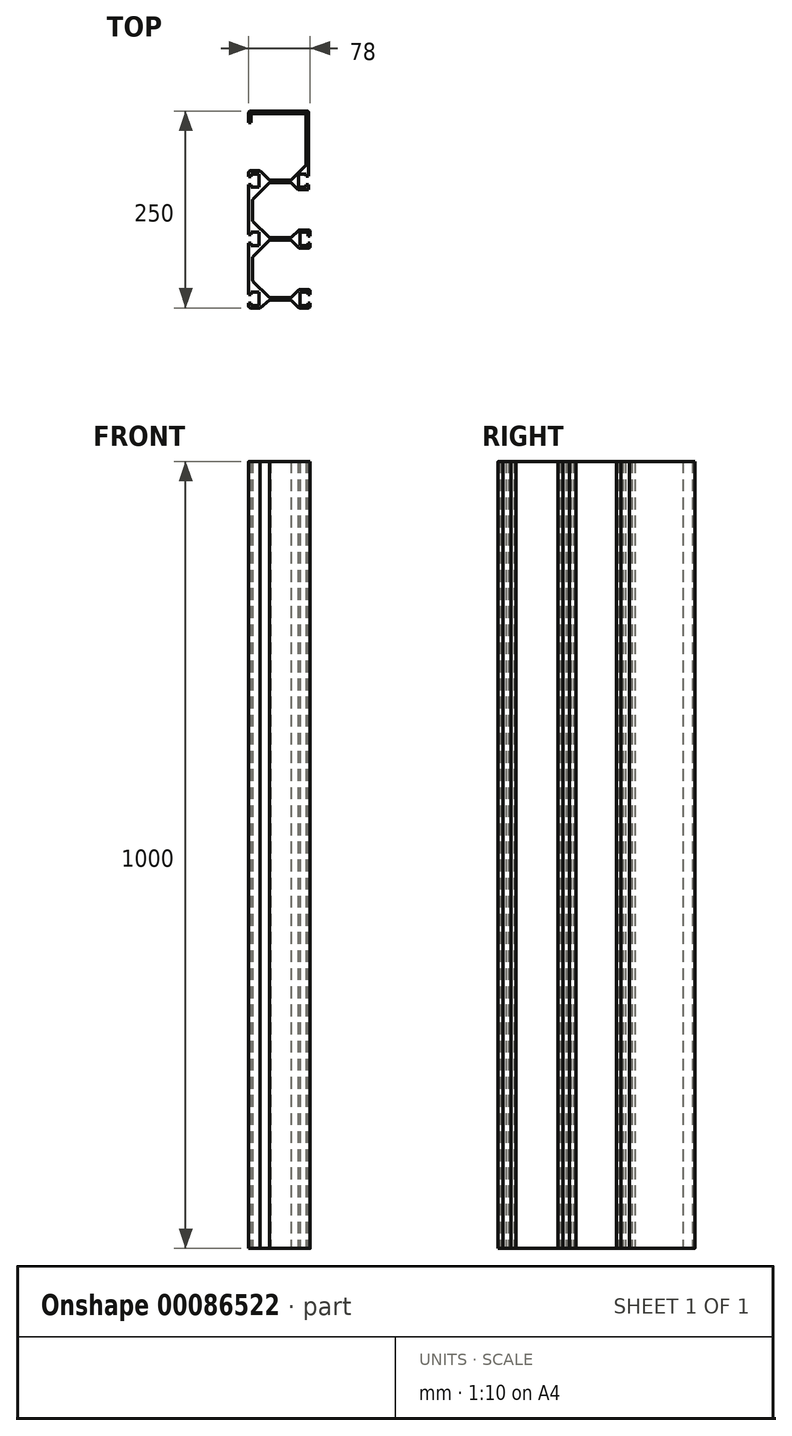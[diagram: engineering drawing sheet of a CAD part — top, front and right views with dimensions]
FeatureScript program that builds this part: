
annotation { "Feature Type Name" : "Feature", "Feature Type Description" : "" }
export const myFeature = defineFeature(function(context is Context, id is Id, definition is map)
    precondition{}
    {
        {
            var Q0;
            Q0=qCreatedBy(makeId("Top.planeOp"),FACE);
            var sketch = newSketch(context, id + "F0", { "sketchPlane" : qUnion([Q0])});
            skLineSegment(sketch, "E0", {"start": v(0, 3.75) * mm, "end": v(3, 3.75) * mm});
            skLineSegment(sketch, "E1", {"start": v(3, 3.75) * mm, "end": v(3, 7) * mm});
            skLineSegment(sketch, "E2", {"start": v(3, 7) * mm, "end": v(13, 7) * mm});
            skPoint(sketch, "E3.visualSharp", {"position": v(16, 0) * mm});
            skLineSegment(sketch, "E4", {"start": v(13, 7) * mm, "end": v(13, -10) * mm});
            skLineSegment(sketch, "E5", {"start": v(13, -10) * mm, "end": v(3, -10) * mm});
            skLineSegment(sketch, "E6", {"start": v(3, -10) * mm, "end": v(3, -6.75) * mm});
            skLineSegment(sketch, "E7", {"start": v(3, -6.75) * mm, "end": v(0, -6.75) * mm});
            skLineSegment(sketch, "E8", {"start": v(13, -67.17) * mm, "end": v(13, -84.17) * mm});
            skLineSegment(sketch, "E9", {"start": v(0, -6.75) * mm, "end": v(0, -70.42) * mm});
            skLineSegment(sketch, "E10", {"start": v(0, -70.42) * mm, "end": v(3, -70.42) * mm});
            skLineSegment(sketch, "E11", {"start": v(3, -70.42) * mm, "end": v(3, -67.17) * mm});
            skLineSegment(sketch, "E12", {"start": v(3, -67.17) * mm, "end": v(13, -67.17) * mm});
            skLineSegment(sketch, "E13", {"start": v(13, -84.17) * mm, "end": v(3, -84.17) * mm});
            skLineSegment(sketch, "E14", {"start": v(3, -84.17) * mm, "end": v(3, -80.92) * mm});
            skLineSegment(sketch, "E15", {"start": v(3, -80.92) * mm, "end": v(0, -80.92) * mm});
            skLineSegment(sketch, "E16", {"start": v(0, -80.92) * mm, "end": v(0, -146.42) * mm});
            skLineSegment(sketch, "E17", {"start": v(0, -146.42) * mm, "end": v(3, -146.42) * mm});
            skLineSegment(sketch, "E18", {"start": v(3, -146.42) * mm, "end": v(3, -143.17) * mm});
            skLineSegment(sketch, "E19", {"start": v(3, -143.17) * mm, "end": v(13, -143.17) * mm});
            skLineSegment(sketch, "E20", {"start": v(13, -143.17) * mm, "end": v(13, -160.17) * mm});
            skLineSegment(sketch, "E21", {"start": v(13, -160.17) * mm, "end": v(3, -160.17) * mm});
            skLineSegment(sketch, "E22", {"start": v(3, -160.17) * mm, "end": v(3, -156.92) * mm});
            skLineSegment(sketch, "E23", {"start": v(3, -156.92) * mm, "end": v(0, -156.92) * mm});
            skLineSegment(sketch, "E24", {"start": v(0, -156.92) * mm, "end": v(0, -161.17) * mm});
            skLineSegment(sketch, "E25", {"start": v(5.59, -129.54) * mm, "end": v(25.63, -149.59) * mm});
            skLineSegment(sketch, "E26", {"start": v(26.2, -77.18) * mm, "end": v(5.59, -97.8) * mm});
            skLineSegment(sketch, "E27", {"start": v(5, -128.13) * mm, "end": v(5, -99.21) * mm});
            skLineSegment(sketch, "E28", {"start": v(25.65, -73.63) * mm, "end": v(5.59, -53.54) * mm});
            skLineSegment(sketch, "E29", {"start": v(5, -26.21) * mm, "end": v(5, -52.13) * mm});
            skLineSegment(sketch, "E30", {"start": v(2, -163.17) * mm, "end": v(14.21, -163.17) * mm});
            skLineSegment(sketch, "E31", {"start": v(14.21, -163.17) * mm, "end": v(26.21, -153.17) * mm});
            skPoint(sketch, "E32.visualSharp", {"position": v(26.21, -150.17) * mm});
            skArc(sketch, "E32.filletArc", {"start": v(25.63, -149.59) * mm, "mid": v(26.28, -150.02) * mm, "end": v(27.04, -150.17) * mm});
            skPoint(sketch, "E33.visualSharp", {"position": v(5, -128.96) * mm});
            skArc(sketch, "E33.filletArc", {"start": v(5, -128.13) * mm, "mid": v(5.15, -128.9) * mm, "end": v(5.59, -129.54) * mm});
            skPoint(sketch, "E34.visualSharp", {"position": v(5, -98.39) * mm});
            skArc(sketch, "E34.filletArc", {"start": v(5.59, -97.8) * mm, "mid": v(5.15, -98.45) * mm, "end": v(5, -99.21) * mm});
            skPoint(sketch, "E35.visualSharp", {"position": v(26.21, -77.17) * mm});
            skArc(sketch, "E35.filletArc", {"start": v(26.21, -77.17) * mm, "mid": v(26.2, -77.18) * mm, "end": v(26.2, -77.18) * mm});
            skPoint(sketch, "E36.visualSharp", {"position": v(26.21, -74.2) * mm});
            skArc(sketch, "E36.filletArc", {"start": v(25.65, -73.63) * mm, "mid": v(26.49, -74.13) * mm, "end": v(27.46, -74.17) * mm});
            skPoint(sketch, "E37.visualSharp", {"position": v(5, -25.38) * mm});
            skArc(sketch, "E37.filletArc", {"start": v(5.59, -24.8) * mm, "mid": v(5.15, -25.45) * mm, "end": v(5, -26.21) * mm});
            skArc(sketch, "E38.filletArc", {"start": v(26.21, -4.17) * mm, "mid": v(26.2, -4.18) * mm, "end": v(26.2, -4.19) * mm});
            skPoint(sketch, "E39.visualSharp", {"position": v(5, -52.96) * mm});
            skArc(sketch, "E39.filletArc", {"start": v(5, -52.13) * mm, "mid": v(5.15, -52.9) * mm, "end": v(5.59, -53.54) * mm});
            skLineSegment(sketch, "E40", {"start": v(76, -163.17) * mm, "end": v(64.62, -163.17) * mm});
            skLineSegment(sketch, "E41", {"start": v(63.2, -162.59) * mm, "end": v(54.37, -153.76) * mm});
            skLineSegment(sketch, "E42", {"start": v(52.96, -153.17) * mm, "end": v(26.21, -153.17) * mm});
            skLineSegment(sketch, "E43", {"start": v(78, -161.17) * mm, "end": v(78, -156.92) * mm});
            skLineSegment(sketch, "E44", {"start": v(78, -156.92) * mm, "end": v(75, -156.92) * mm});
            skLineSegment(sketch, "E45", {"start": v(75, -156.92) * mm, "end": v(75, -160.17) * mm});
            skLineSegment(sketch, "E46", {"start": v(75, -160.17) * mm, "end": v(65, -160.17) * mm});
            skLineSegment(sketch, "E47", {"start": v(65, -160.17) * mm, "end": v(65, -143.17) * mm});
            skLineSegment(sketch, "E48", {"start": v(65, -143.17) * mm, "end": v(75, -143.17) * mm});
            skLineSegment(sketch, "E49", {"start": v(75, -143.17) * mm, "end": v(75, -146.42) * mm});
            skLineSegment(sketch, "E50", {"start": v(75, -146.42) * mm, "end": v(78, -146.42) * mm});
            skLineSegment(sketch, "E51", {"start": v(78, -146.42) * mm, "end": v(78, -142.17) * mm});
            skLineSegment(sketch, "E52", {"start": v(76, -140.17) * mm, "end": v(64.62, -140.17) * mm});
            skLineSegment(sketch, "E53", {"start": v(63.2, -140.76) * mm, "end": v(54.37, -149.59) * mm});
            skLineSegment(sketch, "E54", {"start": v(52.96, -150.17) * mm, "end": v(27.04, -150.17) * mm});
            skPoint(sketch, "E55.visualSharp", {"position": v(53.79, -150.17) * mm});
            skArc(sketch, "E55.filletArc", {"start": v(52.96, -150.17) * mm, "mid": v(53.72, -150.02) * mm, "end": v(54.37, -149.59) * mm});
            skPoint(sketch, "E56.visualSharp", {"position": v(53.79, -153.17) * mm});
            skArc(sketch, "E56.filletArc", {"start": v(54.37, -153.76) * mm, "mid": v(53.72, -153.32) * mm, "end": v(52.96, -153.17) * mm});
            skPoint(sketch, "E57.visualSharp", {"position": v(63.79, -140.17) * mm});
            skArc(sketch, "E57.filletArc", {"start": v(64.62, -140.17) * mm, "mid": v(63.85, -140.32) * mm, "end": v(63.2, -140.76) * mm});
            skPoint(sketch, "E58.visualSharp", {"position": v(63.79, -163.17) * mm});
            skArc(sketch, "E58.filletArc", {"start": v(63.2, -162.59) * mm, "mid": v(63.85, -163.02) * mm, "end": v(64.62, -163.17) * mm});
            skPoint(sketch, "E59.visualSharp", {"position": v(78, -140.17) * mm});
            skArc(sketch, "E59.filletArc", {"start": v(78, -142.17) * mm, "mid": v(77.41, -140.76) * mm, "end": v(76, -140.17) * mm});
            skPoint(sketch, "E60.visualSharp", {"position": v(78, -163.17) * mm});
            skArc(sketch, "E60.filletArc", {"start": v(76, -163.17) * mm, "mid": v(77.41, -162.59) * mm, "end": v(78, -161.17) * mm});
            skPoint(sketch, "E61.visualSharp", {"position": v(0, -163.17) * mm});
            skArc(sketch, "E61.filletArc", {"start": v(0, -161.17) * mm, "mid": v(0.59, -162.59) * mm, "end": v(2, -163.17) * mm});
            skLineSegment(sketch, "E62", {"start": v(64.62, -87.17) * mm, "end": v(76, -87.17) * mm});
            skLineSegment(sketch, "E63", {"start": v(64.62, -64.17) * mm, "end": v(76, -64.17) * mm});
            skLineSegment(sketch, "E64", {"start": v(78, -66.17) * mm, "end": v(78, -72.21) * mm});
            skLineSegment(sketch, "E65", {"start": v(78, -72.21) * mm, "end": v(75, -72.21) * mm});
            skLineSegment(sketch, "E66", {"start": v(75, -72.21) * mm, "end": v(75, -67.17) * mm});
            skLineSegment(sketch, "E67", {"start": v(75, -67.17) * mm, "end": v(65, -67.17) * mm});
            skLineSegment(sketch, "E68", {"start": v(65, -67.17) * mm, "end": v(65, -84.17) * mm});
            skLineSegment(sketch, "E69", {"start": v(65, -84.17) * mm, "end": v(75, -84.17) * mm});
            skLineSegment(sketch, "E70", {"start": v(75, -84.17) * mm, "end": v(75, -80.92) * mm});
            skLineSegment(sketch, "E71", {"start": v(75, -80.92) * mm, "end": v(78, -80.92) * mm});
            skLineSegment(sketch, "E72", {"start": v(78, -80.92) * mm, "end": v(78, -85.17) * mm});
            skLineSegment(sketch, "E73", {"start": v(27.46, -74.17) * mm, "end": v(52.96, -74.17) * mm});
            skLineSegment(sketch, "E74", {"start": v(54.37, -73.59) * mm, "end": v(63.2, -64.76) * mm});
            skLineSegment(sketch, "E75", {"start": v(26.21, -77.17) * mm, "end": v(52.96, -77.17) * mm});
            skLineSegment(sketch, "E76", {"start": v(54.37, -77.76) * mm, "end": v(63.2, -86.59) * mm});
            skPoint(sketch, "E77.visualSharp", {"position": v(63.79, -87.17) * mm});
            skArc(sketch, "E77.filletArc", {"start": v(63.2, -86.59) * mm, "mid": v(63.85, -87.02) * mm, "end": v(64.62, -87.17) * mm});
            skPoint(sketch, "E78.visualSharp", {"position": v(63.79, -64.17) * mm});
            skArc(sketch, "E78.filletArc", {"start": v(64.62, -64.17) * mm, "mid": v(63.85, -64.32) * mm, "end": v(63.2, -64.76) * mm});
            skPoint(sketch, "E79.visualSharp", {"position": v(78, -64.17) * mm});
            skArc(sketch, "E79.filletArc", {"start": v(78, -66.17) * mm, "mid": v(77.41, -64.76) * mm, "end": v(76, -64.17) * mm});
            skPoint(sketch, "E80.visualSharp", {"position": v(78, -87.17) * mm});
            skArc(sketch, "E80.filletArc", {"start": v(76, -87.17) * mm, "mid": v(77.41, -86.59) * mm, "end": v(78, -85.17) * mm});
            skPoint(sketch, "E81.visualSharp", {"position": v(53.79, -74.17) * mm});
            skArc(sketch, "E81.filletArc", {"start": v(52.96, -74.17) * mm, "mid": v(53.72, -74.02) * mm, "end": v(54.37, -73.59) * mm});
            skPoint(sketch, "E82.visualSharp", {"position": v(53.79, -77.17) * mm});
            skArc(sketch, "E82.filletArc", {"start": v(54.37, -77.76) * mm, "mid": v(53.72, -77.32) * mm, "end": v(52.96, -77.17) * mm});
            skLineSegment(sketch, "E83", {"start": v(76, -13) * mm, "end": v(76, -6.75) * mm});
            skLineSegment(sketch, "E84", {"start": v(76, -6.75) * mm, "end": v(73, -6.75) * mm});
            skLineSegment(sketch, "E85", {"start": v(73, -6.75) * mm, "end": v(73, -10) * mm});
            skLineSegment(sketch, "E86", {"start": v(73, -10) * mm, "end": v(63, -10) * mm});
            skLineSegment(sketch, "E87", {"start": v(63, -10) * mm, "end": v(63, 7) * mm});
            skLineSegment(sketch, "E88", {"start": v(63, 7) * mm, "end": v(73, 7) * mm});
            skLineSegment(sketch, "E89", {"start": v(73, 7) * mm, "end": v(73, 4.05) * mm});
            skLineSegment(sketch, "E90", {"start": v(73, 4.05) * mm, "end": v(76, 4.05) * mm});
            skLineSegment(sketch, "E91", {"start": v(53.79, -4.17) * mm, "end": v(62.62, -13) * mm});
            skLineSegment(sketch, "E92", {"start": v(62.62, -13) * mm, "end": v(76, -13) * mm});
            skLineSegment(sketch, "E93", {"start": v(76, 4.05) * mm, "end": v(76, 84.83) * mm});
            skLineSegment(sketch, "E94", {"start": v(74, 86.83) * mm, "end": v(2, 86.83) * mm});
            skLineSegment(sketch, "E95", {"start": v(0, 84.83) * mm, "end": v(0, 71.83) * mm});
            skLineSegment(sketch, "E96", {"start": v(0, 71.83) * mm, "end": v(3, 71.83) * mm});
            skLineSegment(sketch, "E97", {"start": v(3, 71.83) * mm, "end": v(3, 81.83) * mm});
            skLineSegment(sketch, "E98", {"start": v(5, 83.83) * mm, "end": v(71, 83.83) * mm});
            skLineSegment(sketch, "E99", {"start": v(73, 81.83) * mm, "end": v(73, 18.87) * mm});
            skLineSegment(sketch, "E100", {"start": v(72.41, 17.46) * mm, "end": v(54.37, -0.59) * mm});
            skPoint(sketch, "E101.visualSharp", {"position": v(53.79, -1.17) * mm});
            skArc(sketch, "E101.filletArc", {"start": v(52.96, -1.17) * mm, "mid": v(53.72, -1.02) * mm, "end": v(54.37, -0.59) * mm});
            skPoint(sketch, "E102.visualSharp", {"position": v(73, 18.04) * mm});
            skArc(sketch, "E102.filletArc", {"start": v(72.41, 17.46) * mm, "mid": v(72.85, 18.1) * mm, "end": v(73, 18.87) * mm});
            skPoint(sketch, "E103.visualSharp", {"position": v(0, 86.83) * mm});
            skArc(sketch, "E103.filletArc", {"start": v(2, 86.83) * mm, "mid": v(0.59, 86.24) * mm, "end": v(0, 84.83) * mm});
            skPoint(sketch, "E104.visualSharp", {"position": v(76, 86.83) * mm});
            skArc(sketch, "E104.filletArc", {"start": v(76, 84.83) * mm, "mid": v(75.41, 86.24) * mm, "end": v(74, 86.83) * mm});
            skPoint(sketch, "E105.visualSharp", {"position": v(73, 83.83) * mm});
            skArc(sketch, "E105.filletArc", {"start": v(73, 81.83) * mm, "mid": v(72.41, 83.24) * mm, "end": v(71, 83.83) * mm});
            skPoint(sketch, "E106.visualSharp", {"position": v(3, 83.83) * mm});
            skArc(sketch, "E106.filletArc", {"start": v(5, 83.83) * mm, "mid": v(3.59, 83.24) * mm, "end": v(3, 81.83) * mm});
            skLineSegment(sketch, "E107", {"start": v(14.7, 10.33) * mm, "end": v(25.63, -0.59) * mm});
            skLineSegment(sketch, "E108", {"start": v(27.04, -1.17) * mm, "end": v(52.96, -1.17) * mm});
            skLineSegment(sketch, "E109", {"start": v(13.3, 10.92) * mm, "end": v(2, 10.92) * mm});
            skLineSegment(sketch, "E110", {"start": v(0, 8.92) * mm, "end": v(0, 3.75) * mm});
            skPoint(sketch, "E111.visualSharp", {"position": v(14.12, 10.92) * mm});
            skArc(sketch, "E111.filletArc", {"start": v(14.7, 10.33) * mm, "mid": v(14.06, 10.77) * mm, "end": v(13.3, 10.92) * mm});
            skPoint(sketch, "E112.visualSharp", {"position": v(26.21, -1.17) * mm});
            skArc(sketch, "E112.filletArc", {"start": v(25.63, -0.59) * mm, "mid": v(26.28, -1.02) * mm, "end": v(27.04, -1.17) * mm});
            skPoint(sketch, "E113.visualSharp", {"position": v(0, 10.92) * mm});
            skArc(sketch, "E113.filletArc", {"start": v(2, 10.92) * mm, "mid": v(0.59, 10.33) * mm, "end": v(0, 8.92) * mm});
            skLineSegment(sketch, "E114", {"start": v(53.79, -4.17) * mm, "end": v(26.21, -4.17) * mm});
            skLineSegment(sketch, "E115", {"start": v(5.59, -24.8) * mm, "end": v(26.21, -4.17) * mm});
            skSolve(sketch);
        }
        {
            var Q0;
            Q0=makeQuery(id+"F0.imprint","IMPRINT",FACE,{"disambiguationData":[TD([[makeQuery(id+"F0.imprint","IMPRINT",EDGE,{"derivedFrom":sQuery(id+"F0.wireOp",EDGE,"E0")}),1.0]])]});
            extrude(context, id + "F1", {"entities" : qUnion([Q0]), "depth" : 1000 * mm});
        }
    });
